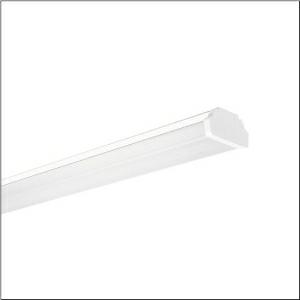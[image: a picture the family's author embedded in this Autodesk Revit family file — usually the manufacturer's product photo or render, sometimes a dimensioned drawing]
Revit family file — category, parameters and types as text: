
# Revit family: dus_31_gen_2_53bd812cv4dxd2_5f47
name_source: partatom
category: Lighting Fixtures
units: mm (PartAtom-declared; Revit-internal decimal feet)

## family parameters
Cut with Voids When Loaded = No
Host = Face
Light Source = No
Part Type = Normal
Room Calculation Point = No
Round Connector Dimension = Use Diameter
Shared = No

## types (1)
- --- (1 x LED, 13040 lm, 68.5 W, 4000K)
    Apparent Load = 69 VA
    CIE Flux Codes = 47 80 95 93 100
    Color Rendering = 80
    Color Temperature = 4000K
    Default Elevation = 1800 mm
    Description = DUS 31 Gen.2, luminaire insert, of sheet steel, coil coated, white, length: 1.535mm, width: 81mm, height: 90mm, 5x system unit, system units: 307mm, LED rated luminous flux: 13.040lm, light colour: 840, SDCM (Standard Deviation of Colour Matching)MacAdam ≤ 3 SDCM (initial), control gear: ON/OFF Multilumen, CLOi, with plug, 3-pole, with phase selection, mains connection: 220..240V, AC, 50/60Hz, start of lifetime: 69W, end of service life: 82W, through-wiring accessed according to module size, primary optical cover: cover, of PMMA, light emission: direct distribution, primary light characteristic: symmetric, protection rating (complete): IP20, protection rating (LED compartment): IP50, insulation class (complete): insulation class I (protective earthing), certification: CE, ENEC, VDE, UKCA, impact resistance: IK03, permissible ambient temperature for indoor applications: -35..+35°C, corresponds to IFS (International Featured Standards) requirements for safety and quality in the food industry, reducing of maximum allowable ambient temperature of 5°C with ceiling mounting, packaging unit: 1 piece
    Height = 95 mm
    Lamp = 1 x LED
    Lamp Light Flux = 13040 lm
    Lamp Power = 68.5 W
    Lamp count = 1
    Length = 1535 mm
    Luminous efficacy = 190 lm/W
    Manufacturer = Siteco
    ModVariant = No
    Model = 53BD812CV4DXD2
    Mounting Place = Ceiling
    Mounting Type = Pendant
    Number of Poles = 1
    OnlyDefault = Yes
    Power Factor = 1
    Product Name = DUS 31 Gen.2
    Product group = luminaire insert | ceiling pendant
    ProductGroupID = 901
    Protection Class = Protection class I
    Protection Degree = IP 20
    RLX_Detail_Level = 1
    RLX_Emergency_Light_Flux = 0 lm
    RLX_Emergency_Type = 0
    RLX_Emergency_Type_DB = No
    RlxData = <blob elided: 29957 chars, md5=b5882b23>
    Socket = socket
    Standby Power = 0 W
    System Light Flux = 13040 lm
    System Power = 69 W
    Type Comments = factory setting: luminous flux: 100 % | (A | C | E) | 161 mA
    Type Image = l_1319596.jpg
    URL = http://relux.com
    VarID = @adj_049659
    Voltage = 0 V
    Weight = 0.00 kg
    Width = 81 mm

## geometry (parser evidence)
native form markers: Blend x4, Sweep x11
no freeform markers — native parametric forms only
